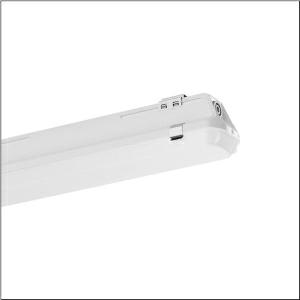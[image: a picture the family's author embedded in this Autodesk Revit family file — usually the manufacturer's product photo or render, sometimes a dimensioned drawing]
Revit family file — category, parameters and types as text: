
# Revit family: monsun_r__11_51fp20dp4b0q_5d72
name_source: partatom
category: Lighting Fixtures
units: mm (PartAtom-declared; Revit-internal decimal feet)

## family parameters
Cut with Voids When Loaded = No
Host = Face
Light Source = No
Part Type = Normal
Room Calculation Point = No
Round Connector Dimension = Use Diameter
Shared = No

## types (1)
- --- (1 x LED, 10950 lm, 67.6 W, 4000K)
    Apparent Load = 68 VA
    CIE Flux Codes = 45 75 93 94 100
    Color Rendering = 80
    Color Temperature = 4000K
    Default Elevation = 1800 mm
    Description = Monsun® 11, damp-proof luminaire, chain hanger, primary optical cover: enclosure, of PC, light emission: direct distribution, primary light characteristic: symmetric, installation type: suspended mounting, surface-mounted, horizontal mounting, vertical mounting, LED, rated luminous flux: 10.950lm, luminous efficacy: 162lm/W, light colour: 840, colour temperature: 4000K, control gear: ECG DALI, with terminal, 5-pole, max. 2.5mm², mains connection: 220..240V, AC, 50/60Hz, rated input power: 68W, luminaire housing, of glass-fibre reinforced polyester, uncoated, bright grey, incl. chain hanger, length: 1.590mm, width: 90mm, height: 88mm, clip for enclosure, of stainless steel (V2A), ceiling mounting element, of stainless steel (V2A), chain hanger, of stainless steel (V2A), protection rating (complete): IP66, insulation class (complete): insulation class I (protective earthing), certification: CE, ENEC, VDE, UKCA, protection symbol: D, impact resistance: IK08, permissible operating ambient temperature: -40..+35°C, standard: EN 50419, EN 60598-2-1, no direct snow, no direct sun, no direct rain, for indoor or canopied outdoor use, corresponds to IFS (International Featured Standards) requirements for safety and quality in the food industry, contact your sales advisor before using the luminaires in applications with unclear chemical exposure, large temperature fluctuations or condensation-forming humidity, LABS conformity tested according to VDMA 24364:2018-05, packaging unit: 1 piece
    Height = 89 mm
    Lamp = 1 x LED
    Lamp Light Flux = 10950 lm
    Lamp Power = 67.6 W
    Lamp count = 1
    Length = 1590 mm
    Luminous efficacy = 162 lm/W
    Manufacturer = Siteco
    ModVariant = No
    Model = 51FP20DP4B0Q
    Mounting Place = Ceiling
    Mounting Type = Surface mounted
    Number of Poles = 1
    OnlyDefault = Yes
    Power Factor = 1
    Product Name = Monsun® 11
    Product group = damp-proof luminaire
    ProductGroupID = 300
    Protection Class = Protection class I
    Protection Degree = IP 66
    RLX_Detail_Level = 1
    RLX_Emergency_Light_Flux = 0 lm
    RLX_Emergency_Type = 0
    RLX_Emergency_Type_DB = No
    RlxData = <blob elided: 91909 chars, md5=72735a3a>
    Socket = socket
    Standby Power = 0 W
    System Light Flux = 10950 lm
    System Power = 68 W
    Type Comments = factory setting: luminous flux: 100 % | dim-lin: 254 | 389 mA
    Type Image = l_1004748.jpg
    URL = http://relux.com
    VarID = @adj_140461
    Voltage = 0 V
    Weight = 0.00 kg
    Width = 90 mm

## geometry (parser evidence)
native form markers: Blend x4, Sweep x14
no freeform markers — native parametric forms only
